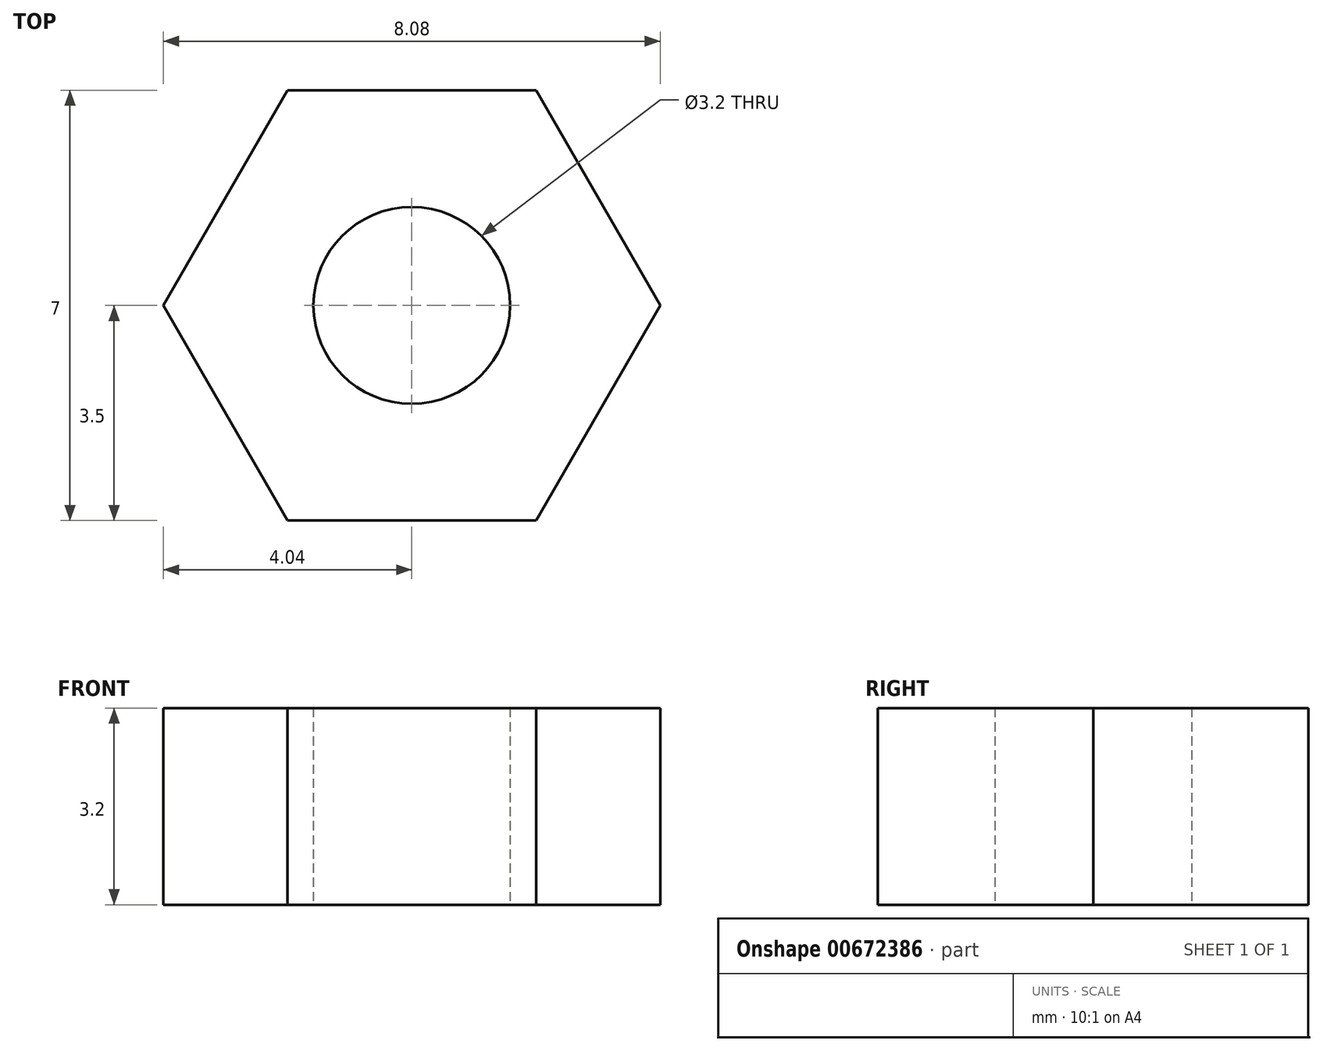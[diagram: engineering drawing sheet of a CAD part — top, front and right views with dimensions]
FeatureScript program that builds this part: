
annotation { "Feature Type Name" : "Feature", "Feature Type Description" : "" }
export const myFeature = defineFeature(function(context is Context, id is Id, definition is map)
    precondition{}
    {
        {
            var Q0;
            Q0=qCreatedBy(makeId("Top.planeOp"),FACE);
            var sketch = newSketch(context, id + "F0", { "sketchPlane" : qUnion([Q0])});
            skCircle(sketch, "E0", {"center": v(0, 0) * mm, "radius": 1.6 * mm});
            skCircle(sketch, "E1.cCircle", {"center": v(0, 0) * mm, "radius": 3.5 * mm, "construction": true});
            skLineSegment(sketch, "E1.0", {"start": v(2.02, -3.5) * mm, "end": v(-2.02, -3.5) * mm});
            skLineSegment(sketch, "E1.1", {"start": v(-2.02, -3.5) * mm, "end": v(-4.04, 0) * mm});
            skLineSegment(sketch, "E1.2", {"start": v(-4.04, 0) * mm, "end": v(-2.02, 3.5) * mm});
            skLineSegment(sketch, "E1.3", {"start": v(-2.02, 3.5) * mm, "end": v(2.02, 3.5) * mm});
            skLineSegment(sketch, "E1.4", {"start": v(2.02, 3.5) * mm, "end": v(4.04, 0) * mm});
            skLineSegment(sketch, "E1.5", {"start": v(4.04, 0) * mm, "end": v(2.02, -3.5) * mm});
            skPoint(sketch, "E1.0.midPoint", {"position": v(0, -3.5) * mm});
            skSolve(sketch);
        }
        {
            var Q0;
            Q0 = qSketchRegion(id + "F0", true);
            extrude(context, id + "F1", {"entities" : qUnion([Q0]), "depth" : 3.2 * mm, "offsetDistance" : 25 * mm});
        }
    });
